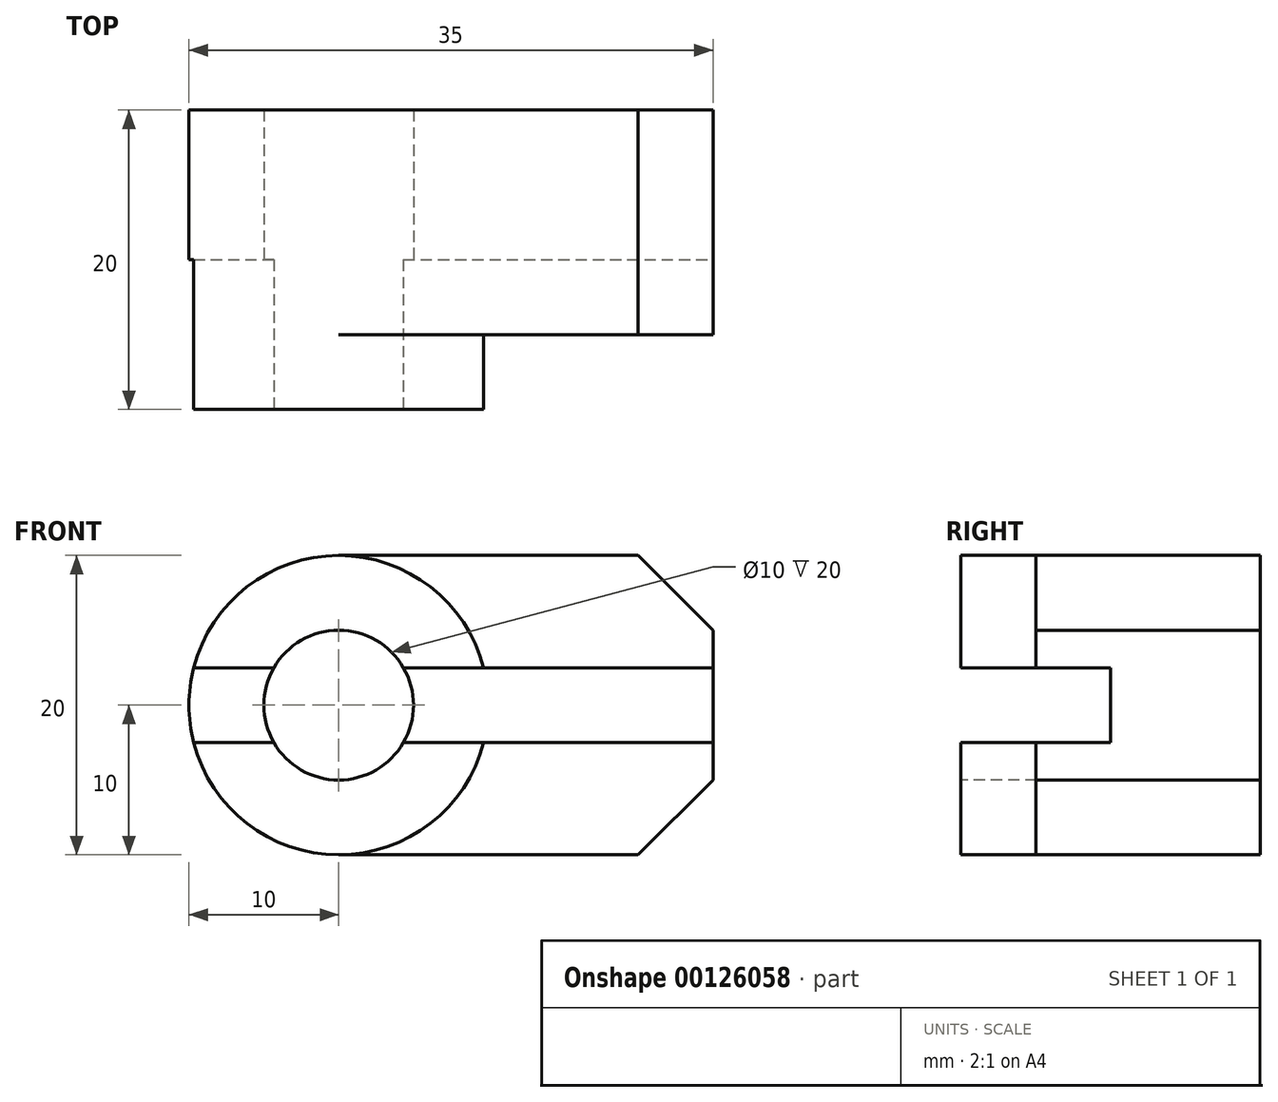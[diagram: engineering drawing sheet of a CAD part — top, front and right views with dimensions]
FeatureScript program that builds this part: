
annotation { "Feature Type Name" : "Feature", "Feature Type Description" : "" }
export const myFeature = defineFeature(function(context is Context, id is Id, definition is map)
    precondition{}
    {
        {
            var Q0;
            Q0=qCreatedBy(makeId("Front.planeOp"),FACE);
            var sketch = newSketch(context, id + "F0", { "sketchPlane" : qUnion([Q0])});
            skCircle(sketch, "E0", {"center": v(0, 0) * mm, "radius": 5 * mm});
            skCircle(sketch, "E1", {"center": v(0, 0) * mm, "radius": 10 * mm});
            skSolve(sketch);
        }
        {
            var Q0;
            Q0 = qSketchRegion(id + "F0", true);
            extrude(context, id + "F1", {"entities" : qUnion([Q0]), "endBound" : BoundingType.SYMMETRIC, "oppositeDirection" : true, "depth" : 20 * mm});
        }
        {
            var Q0;
            Q0=makeQuery(id+"F1.opExtrude","CAP_FACE",FACE,{"disambiguationData":[OSD([sQuery(id+"F0.wireOp",EDGE,"E0"),sQuery(id+"F0.wireOp",EDGE,"E1")])],"isStart":false});
            var sketch = newSketch(context, id + "F2", { "sketchPlane" : qUnion([Q0])});
            skLineSegment(sketch, "E2", {"start": v(0, 10) * mm, "end": v(-20, 10) * mm});
            skLineSegment(sketch, "E3", {"start": v(-20, 10) * mm, "end": v(-25, 5) * mm});
            skLineSegment(sketch, "E4", {"start": v(-25, 5) * mm, "end": v(-25, -5) * mm});
            skLineSegment(sketch, "E5", {"start": v(-25, -5) * mm, "end": v(-20, -10) * mm});
            skLineSegment(sketch, "E6", {"start": v(-20, -10) * mm, "end": v(0, -10) * mm});
            skArc(sketch, "E7.0", {"start": v(0, 10) * mm, "mid": v(-10, 0) * mm, "end": v(0, -10) * mm});
            skPoint(sketch, "E8", {"position": v(0, 10) * mm});
            skPoint(sketch, "E9", {"position": v(0, -10) * mm});
            skSolve(sketch);
        }
        {
            var Q0;
            Q0 = qSketchRegion(id + "F2", true);
            extrude(context, id + "F3", {"entities" : qUnion([Q0]), "operationType" : NewBodyOperationType.ADD, "oppositeDirection" : true, "depth" : 15 * mm});
        }
        {
            var Q0;
            Q0=makeQuery(id+"F3.opExtrude","SWEPT_FACE",FACE,{"disambiguationData":[OSD([sQuery(id+"F2.wireOp",EDGE,"E4")])]});
            var sketch = newSketch(context, id + "F4", { "sketchPlane" : qUnion([Q0])});
            skLineSegment(sketch, "E10.0", {"start": v(-10, -10) * mm, "end": v(-10, 10) * mm});
            skLineSegment(sketch, "E11", {"start": v(-10, 2.5) * mm, "end": v(0, 2.5) * mm});
            skLineSegment(sketch, "E12", {"start": v(0, 2.5) * mm, "end": v(0, -2.5) * mm});
            skLineSegment(sketch, "E13", {"start": v(0, -2.5) * mm, "end": v(-10, -2.5) * mm});
            skLineSegment(sketch, "E14", {"start": v(-10, -2.5) * mm, "end": v(-10, 2.5) * mm});
            skSolve(sketch);
        }
        {
            var Q0;
            Q0 = qSketchRegion(id + "F4", true);
            extrude(context, id + "F5", {"entities" : qUnion([Q0]), "operationType" : NewBodyOperationType.REMOVE, "endBound" : BoundingType.THROUGH_ALL, "oppositeDirection" : true, "depth" : 25 * mm});
        }
    });
